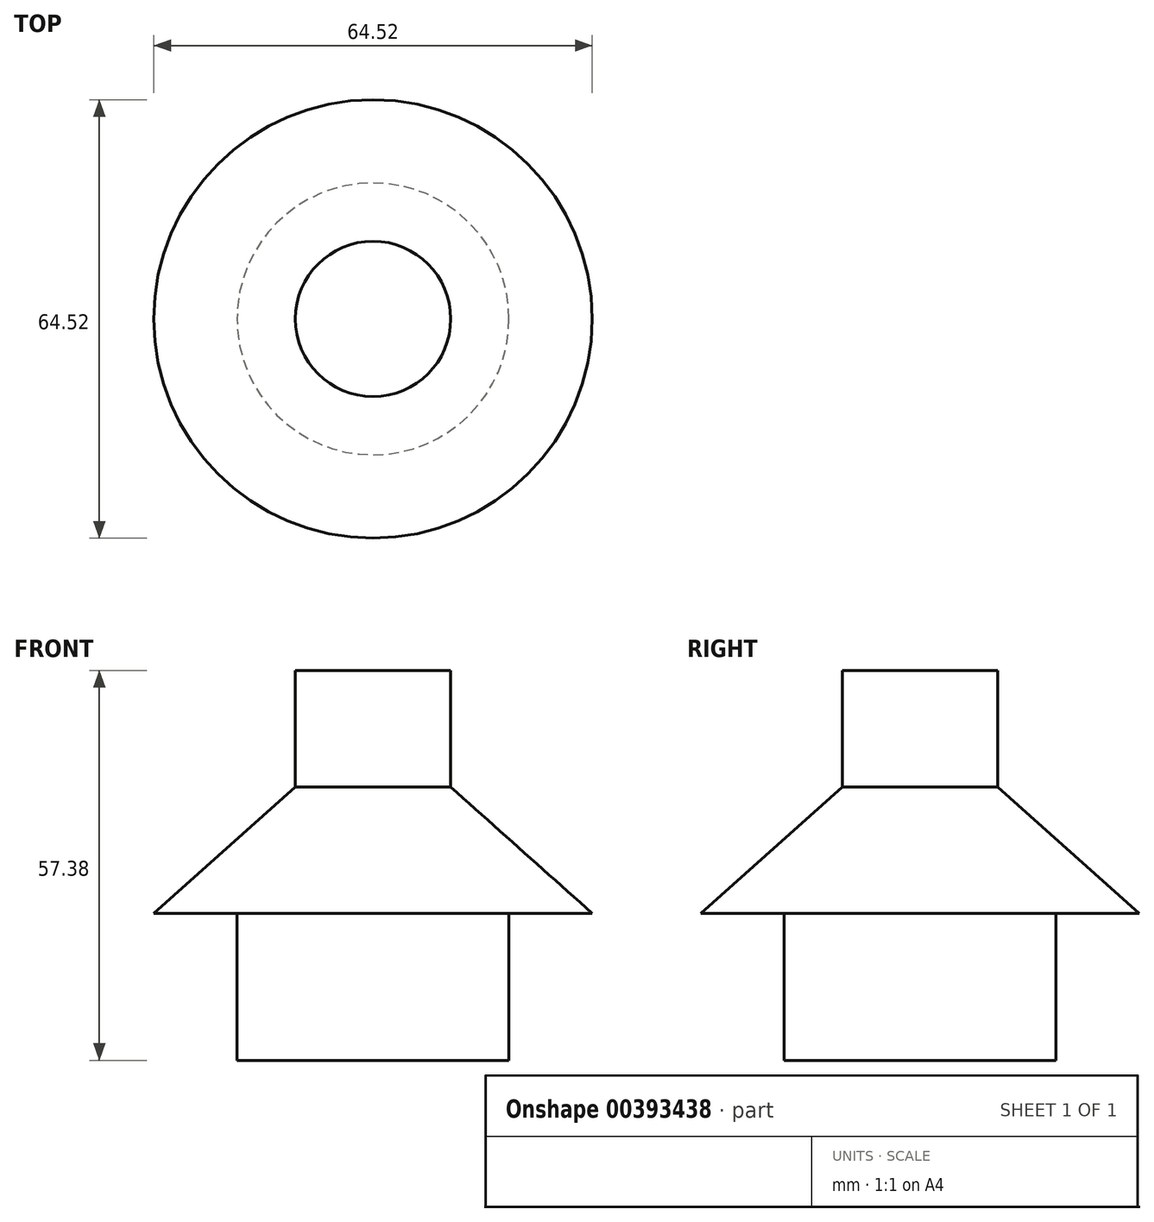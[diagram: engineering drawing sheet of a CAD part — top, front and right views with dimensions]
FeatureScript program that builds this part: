
annotation { "Feature Type Name" : "Feature", "Feature Type Description" : "" }
export const myFeature = defineFeature(function(context is Context, id is Id, definition is map)
    precondition{}
    {
        {
            var Q0;
            Q0=qCreatedBy(makeId("Front.planeOp"),FACE);
            var sketch = newSketch(context, id + "F0", { "sketchPlane" : qUnion([Q0])});
            skLineSegment(sketch, "E0", {"start": v(-20.01, 0) * mm, "end": v(-20.01, 21.64) * mm});
            skLineSegment(sketch, "E1", {"start": v(-20.01, 21.64) * mm, "end": v(-32.26, 21.64) * mm});
            skLineSegment(sketch, "E2", {"start": v(-32.26, 21.64) * mm, "end": v(-11.43, 40.23) * mm});
            skLineSegment(sketch, "E3", {"start": v(-11.43, 40.23) * mm, "end": v(-11.43, 57.38) * mm});
            skLineSegment(sketch, "E4", {"start": v(-11.43, 57.38) * mm, "end": v(0, 57.38) * mm});
            skLineSegment(sketch, "E5", {"start": v(0, 57.38) * mm, "end": v(0, 0) * mm});
            skLineSegment(sketch, "E6", {"start": v(0, 0) * mm, "end": v(-20.01, 0) * mm});
            skSolve(sketch);
        }
        {
            var Q0;
            Q0=makeQuery(id+"F0.imprint","IMPRINT",FACE,{"disambiguationData":[TD([[makeQuery(id+"F0.imprint","IMPRINT",EDGE,{"derivedFrom":sQuery(id+"F0.wireOp",EDGE,"E0")}),-1.0]])]});
            var Q1;
            Q1=sQuery(id+"F0.wireOp",EDGE,"E5");
            revolve(context, id + "F1", {"entities" : qUnion([Q0]), "axis" : qUnion([Q1]), "revolveType" : RevolveType.FULL});
        }
    });
